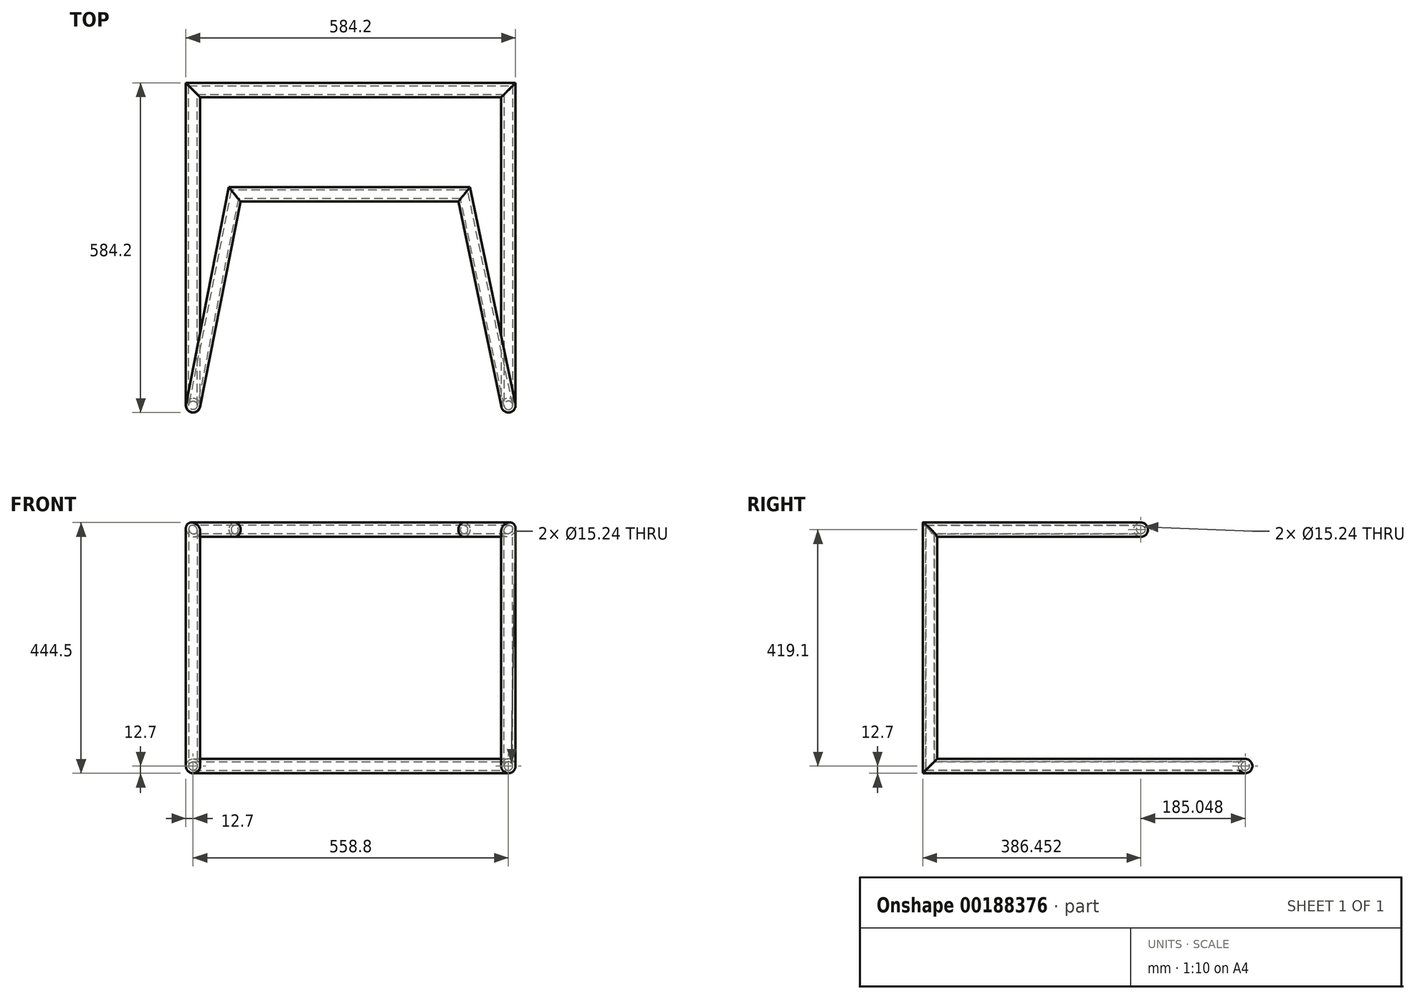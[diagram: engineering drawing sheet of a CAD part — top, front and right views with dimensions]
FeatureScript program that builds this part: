
annotation { "Feature Type Name" : "Feature", "Feature Type Description" : "" }
export const myFeature = defineFeature(function(context is Context, id is Id, definition is map)
    precondition{}
    {
        {
            var Q0;
            Q0=qCreatedBy(makeId("Top.planeOp"),FACE);
            var sketch = newSketch(context, id + "F0", { "sketchPlane" : qUnion([Q0])});
            skLineSegment(sketch, "E0", {"start": v(279.4, 0) * mm, "end": v(-279.4, 0) * mm});
            skLineSegment(sketch, "E1", {"start": v(279.4, 0) * mm, "end": v(279.4, -558.8) * mm});
            skLineSegment(sketch, "E2", {"start": v(-279.4, 0) * mm, "end": v(-279.4, -558.8) * mm});
            skSolve(sketch);
        }
        {
            var Q0;
            Q0=qCreatedBy(makeId("Front.planeOp"),FACE);
            cPlane(context, id + "F1", {"entities" : qUnion([Q0]), "cplaneType" : CPlaneType.OFFSET, "offset" : 558.8 * mm, "width" : 152.4 * mm, "height" : 152.4 * mm});
        }
        {
            var Q0;
            Q0=qCreatedBy(id+"F1.planeOp",FACE);
            var sketch = newSketch(context, id + "F2", { "sketchPlane" : qUnion([Q0])});
            skPoint(sketch, "E3.0", {"position": v(-279.4, 0) * mm});
            skPoint(sketch, "E4.0", {"position": v(279.4, 0) * mm});
            skLineSegment(sketch, "E5", {"start": v(-279.4, 0) * mm, "end": v(-279.4, 419.1) * mm});
            skLineSegment(sketch, "E6", {"start": v(279.4, 0) * mm, "end": v(279.4, 419.1) * mm});
            skSolve(sketch);
        }
        {
            var Q0;
            Q0=qCreatedBy(makeId("Top.planeOp"),FACE);
            cPlane(context, id + "F3", {"entities" : qUnion([Q0]), "cplaneType" : CPlaneType.OFFSET, "offset" : 419.1 * mm, "width" : 152.4 * mm, "height" : 152.4 * mm});
        }
        {
            var Q0;
            Q0=qCreatedBy(id+"F3.planeOp",FACE);
            var sketch = newSketch(context, id + "F4", { "sketchPlane" : qUnion([Q0])});
            skPoint(sketch, "E7.0", {"position": v(-279.4, -558.8) * mm});
            skPoint(sketch, "E8.0", {"position": v(279.4, -558.8) * mm});
            skLineSegment(sketch, "E9", {"start": v(-205.44, -185.05) * mm, "end": v(200.96, -185.05) * mm});
            skLineSegment(sketch, "E10", {"start": v(-279.4, -558.8) * mm, "end": v(-205.44, -185.05) * mm});
            skLineSegment(sketch, "E11", {"start": v(279.4, -558.8) * mm, "end": v(200.96, -185.05) * mm});
            skSolve(sketch);
        }
        {
            var Q0;
            Q0=qCreatedBy(makeId("Right.planeOp"),FACE);
            var sketch = newSketch(context, id + "F5", { "sketchPlane" : qUnion([Q0])});
            skCircle(sketch, "E12", {"center": v(0, 0) * mm, "radius": 12.7 * mm});
            skSolve(sketch);
        }
        {
            var Q0;
            Q0=makeQuery(id+"F5.imprint","IMPRINT",FACE,{"disambiguationData":[TD([[makeQuery(id+"F5.imprint","IMPRINT",EDGE,{"derivedFrom":sQuery(id+"F5.wireOp",EDGE,"E12")}),1.0]])]});
            var Q1;
            Q1=sQuery(id+"F0.wireOp",EDGE,"E0");
            var Q2;
            Q2=sQuery(id+"F0.wireOp",EDGE,"E2");
            var Q3;
            Q3=sQuery(id+"F2.wireOp",EDGE,"E5");
            var Q4;
            Q4=sQuery(id+"F4.wireOp",EDGE,"E10");
            var Q5;
            Q5=sQuery(id+"F4.wireOp",EDGE,"E9");
            var Q6;
            Q6=sQuery(id+"F4.wireOp",EDGE,"E11");
            var Q7;
            Q7=sQuery(id+"F2.wireOp",EDGE,"E6");
            var Q8;
            Q8=sQuery(id+"F0.wireOp",EDGE,"E1");
            sweep(context, id + "F6", {"profiles" : qUnion([Q0]), "path" : qUnion([Q1, Q2, Q3, Q4, Q5, Q6, Q7, Q8])});
        }
        {
            var Q0;
            Q0=qCreatedBy(makeId("Right.planeOp"),FACE);
            var sketch = newSketch(context, id + "F7", { "sketchPlane" : qUnion([Q0])});
            skCircle(sketch, "E13", {"center": v(0, 0) * mm, "radius": 7.62 * mm});
            skSolve(sketch);
        }
        {
            var Q0;
            Q0 = qSketchRegion(id + "F7", true);
            var Q1;
            Q1=sQuery(id+"F0.wireOp",EDGE,"E0");
            var Q2;
            Q2=sQuery(id+"F0.wireOp",EDGE,"E2");
            var Q3;
            Q3=sQuery(id+"F2.wireOp",EDGE,"E5");
            var Q4;
            Q4=sQuery(id+"F4.wireOp",EDGE,"E10");
            var Q5;
            Q5=sQuery(id+"F4.wireOp",EDGE,"E9");
            var Q6;
            Q6=sQuery(id+"F4.wireOp",EDGE,"E11");
            var Q7;
            Q7=sQuery(id+"F2.wireOp",EDGE,"E6");
            var Q8;
            Q8=sQuery(id+"F0.wireOp",EDGE,"E1");
            sweep(context, id + "F8", {"operationType" : NewBodyOperationType.REMOVE, "profiles" : qUnion([Q0]), "path" : qUnion([Q1, Q2, Q3, Q4, Q5, Q6, Q7, Q8])});
        }
    });
